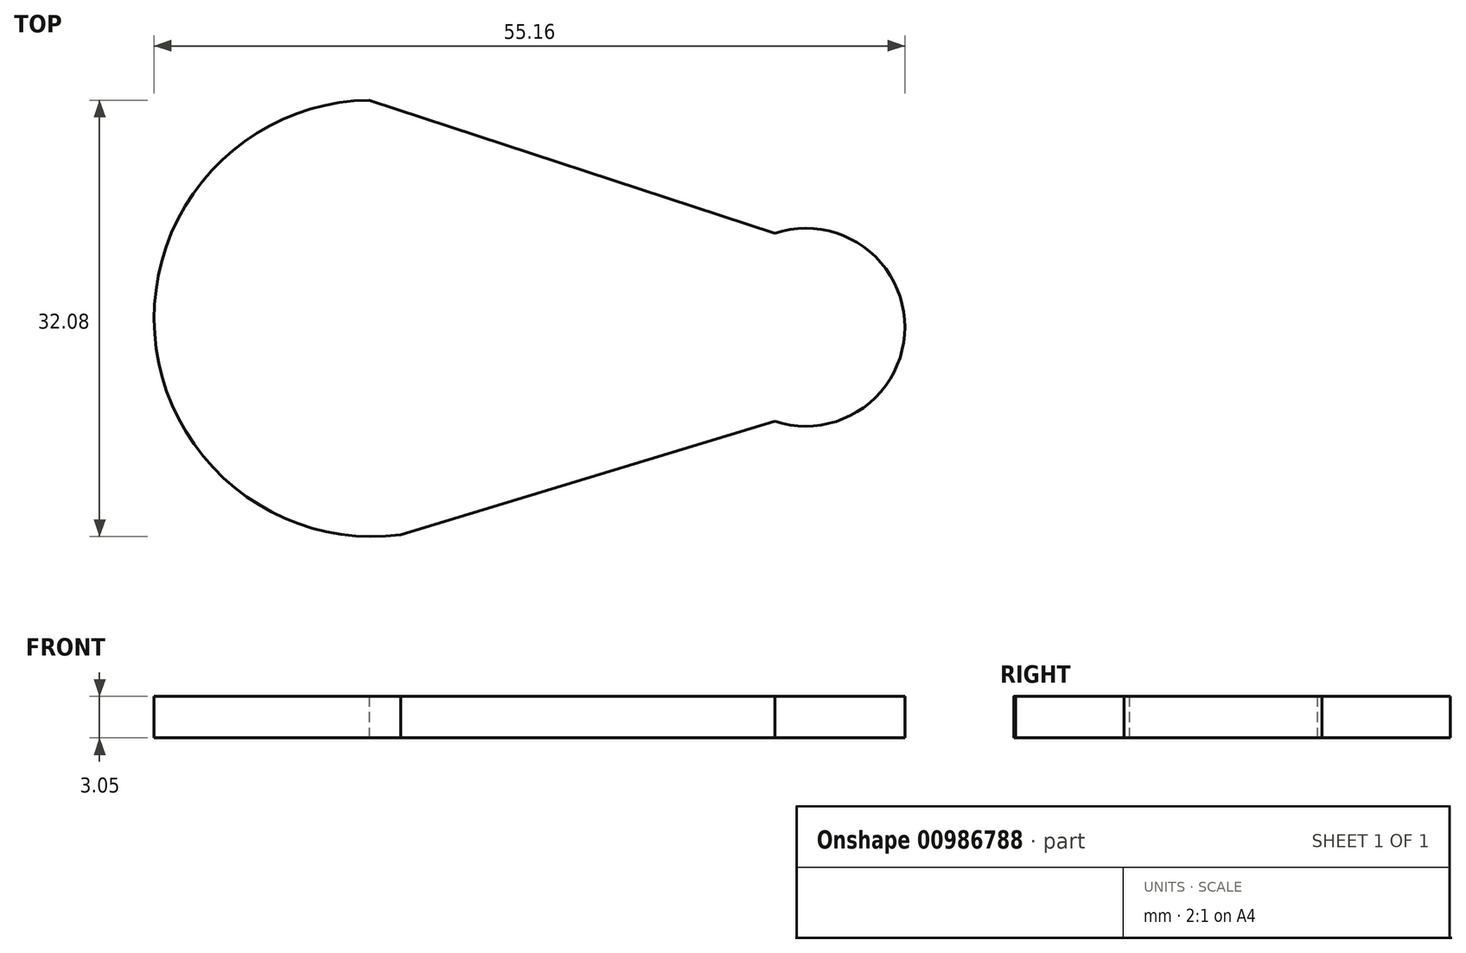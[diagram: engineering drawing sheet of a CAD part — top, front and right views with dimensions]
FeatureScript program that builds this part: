
annotation { "Feature Type Name" : "Feature", "Feature Type Description" : "" }
export const myFeature = defineFeature(function(context is Context, id is Id, definition is map)
    precondition{}
    {
        {
            var Q0;
            Q0=qCreatedBy(makeId("Top.planeOp"),FACE);
            var sketch = newSketch(context, id + "F0", { "sketchPlane" : qUnion([Q0])});
            skArc(sketch, "E0", {"start": v(-29.79, 42.74) * mm, "mid": v(-45.56, 25.55) * mm, "end": v(-27.49, 10.8) * mm});
            skLineSegment(sketch, "E1", {"start": v(-29.79, 42.74) * mm, "end": v(-27.49, 10.8) * mm});
            skLineSegment(sketch, "E2", {"start": v(-29.56, 26.7) * mm, "end": v(-45.56, 25.55) * mm});
            skLineSegment(sketch, "E3", {"start": v(-29.79, 42.74) * mm, "end": v(0, 32.95) * mm});
            skLineSegment(sketch, "E4", {"start": v(-27.49, 10.8) * mm, "end": v(0, 19.14) * mm});
            skArc(sketch, "E5", {"start": v(0, 19.14) * mm, "mid": v(9.56, 26.05) * mm, "end": v(0, 32.95) * mm});
            skLineSegment(sketch, "E6", {"start": v(0, 32.95) * mm, "end": v(0, 19.14) * mm});
            skSolve(sketch);
        }
        {
            var Q0;
            Q0 = qSketchRegion(id + "F0", true);
            extrude(context, id + "F1", {"entities" : qUnion([Q0]), "depth" : 3.05 * mm, "offsetDistance" : 25.4 * mm});
        }
    });
